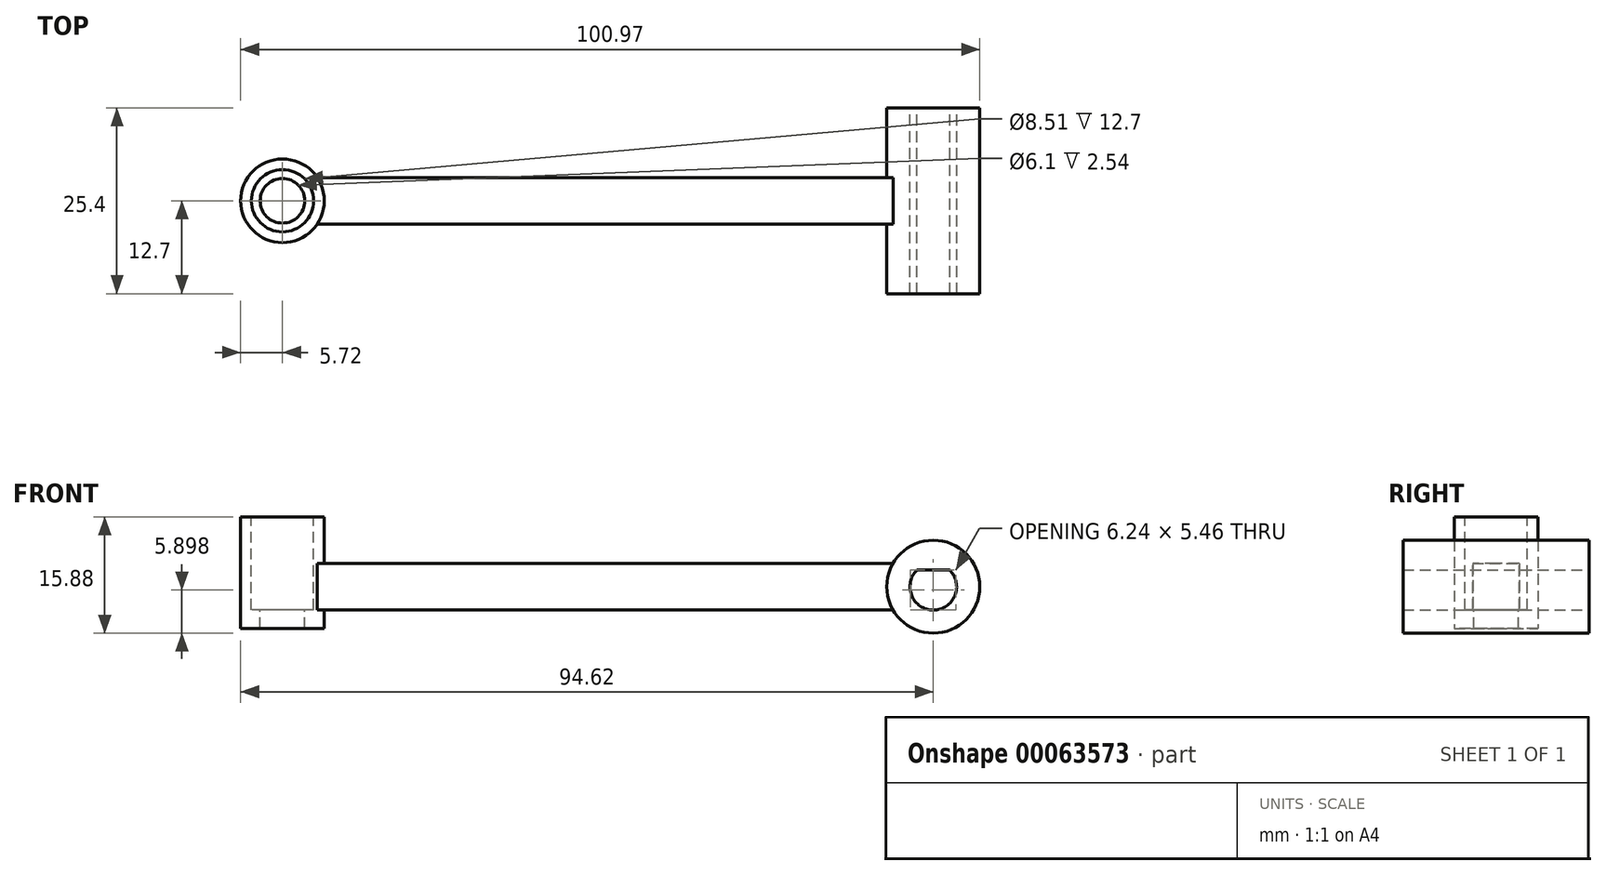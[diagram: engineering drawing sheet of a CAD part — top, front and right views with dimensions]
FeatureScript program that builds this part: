
annotation { "Feature Type Name" : "Feature", "Feature Type Description" : "" }
export const myFeature = defineFeature(function(context is Context, id is Id, definition is map)
    precondition{}
    {
        {
            var Q0;
            Q0=qCreatedBy(makeId("Top.planeOp"),FACE);
            var sketch = newSketch(context, id + "F0", { "sketchPlane" : qUnion([Q0])});
            skCircle(sketch, "E0", {"center": v(0, 0) * mm, "radius": 5.72 * mm});
            skSolve(sketch);
        }
        {
            var Q0;
            Q0 = qSketchRegion(id + "F0", true);
            extrude(context, id + "F1", {"entities" : qUnion([Q0]), "depth" : 15.24 * mm});
        }
        {
            var Q0;
            Q0=makeQuery(id+"F1.opExtrude","CAP_FACE",FACE,{"disambiguationData":[OSD([sQuery(id+"F0.wireOp",EDGE,"E0")])],"isStart":false});
            var sketch = newSketch(context, id + "F2", { "sketchPlane" : qUnion([Q0])});
            skCircle(sketch, "E1", {"center": v(0, 0) * mm, "radius": 4.25 * mm});
            skSolve(sketch);
        }
        {
            var Q0;
            Q0 = qSketchRegion(id + "F2", true);
            extrude(context, id + "F3", {"entities" : qUnion([Q0]), "operationType" : NewBodyOperationType.REMOVE, "oppositeDirection" : true, "depth" : 12.7 * mm});
        }
        {
            var Q0;
            Q0=qCreatedBy(makeId("Right.planeOp"),FACE);
            cPlane(context, id + "F4", {"entities" : qUnion([Q0]), "cplaneType" : CPlaneType.OFFSET, "offset" : 50.8 * mm, "width" : 152.4 * mm, "height" : 152.4 * mm});
        }
        {
            var Q0;
            Q0=qCreatedBy(id+"F4.planeOp",FACE);
            var sketch = newSketch(context, id + "F5", { "sketchPlane" : qUnion([Q0])});
            skLineSegment(sketch, "E2.bottom", {"start": v(-3.17, 8.9) * mm, "end": v(3.18, 8.9) * mm});
            skLineSegment(sketch, "E2.top", {"start": v(-3.17, 2.54) * mm, "end": v(3.18, 2.54) * mm});
            skLineSegment(sketch, "E2.left", {"start": v(-3.17, 8.9) * mm, "end": v(-3.17, 2.54) * mm});
            skLineSegment(sketch, "E2.right", {"start": v(3.18, 8.9) * mm, "end": v(3.18, 2.54) * mm});
            skSolve(sketch);
        }
        {
            var Q0;
            Q0=makeQuery(id+"F3.boolean.opBoolean","COPY",FACE,{"derivedFrom":makeQuery(id+"F3.opExtrude","CAP_FACE",FACE,{"disambiguationData":[OSD([sQuery(id+"F2.wireOp",EDGE,"E1")])],"isStart":false})});
            var sketch = newSketch(context, id + "F6", { "sketchPlane" : qUnion([Q0])});
            skCircle(sketch, "E3", {"center": v(0, 0) * mm, "radius": 3.05 * mm});
            skSolve(sketch);
        }
        {
            var Q0;
            Q0 = qSketchRegion(id + "F6", true);
            extrude(context, id + "F7", {"entities" : qUnion([Q0]), "operationType" : NewBodyOperationType.REMOVE, "endBound" : BoundingType.THROUGH_ALL, "oppositeDirection" : true, "depth" : 25.4 * mm});
        }
        {
            var Q0;
            Q0=qCreatedBy(makeId("Front.planeOp"),FACE);
            var sketch = newSketch(context, id + "F8", { "sketchPlane" : qUnion([Q0])});
            skCircle(sketch, "E4", {"center": v(88.9, 5.72) * mm, "radius": 6.35 * mm});
            skArc(sketch, "E5", {"start": v(86.67, 7.99) * mm, "mid": v(88.9, 2.53) * mm, "end": v(91.13, 7.99) * mm});
            skLineSegment(sketch, "E6", {"start": v(86.67, 7.99) * mm, "end": v(91.13, 7.99) * mm});
            skSolve(sketch);
        }
        {
            var Q0;
            Q0 = qSketchRegion(id + "F8", true);
            extrude(context, id + "F9", {"entities" : qUnion([Q0]), "endBound" : BoundingType.SYMMETRIC, "depth" : 25.4 * mm});
        }
        {
            var Q0;
            Q0 = qSketchRegion(id + "F5", true);
            extrude(context, id + "F10", {"entities" : qUnion([Q0]), "operationType" : NewBodyOperationType.ADD, "endBound" : BoundingType.UP_TO_NEXT, "depth" : 25.4 * mm});
        }
        {
            var Q0;
            Q0 = qSketchRegion(id + "F5", true);
            extrude(context, id + "F11", {"entities" : qUnion([Q0]), "operationType" : NewBodyOperationType.ADD, "endBound" : BoundingType.UP_TO_NEXT, "oppositeDirection" : true, "depth" : 25.4 * mm});
        }
    });
